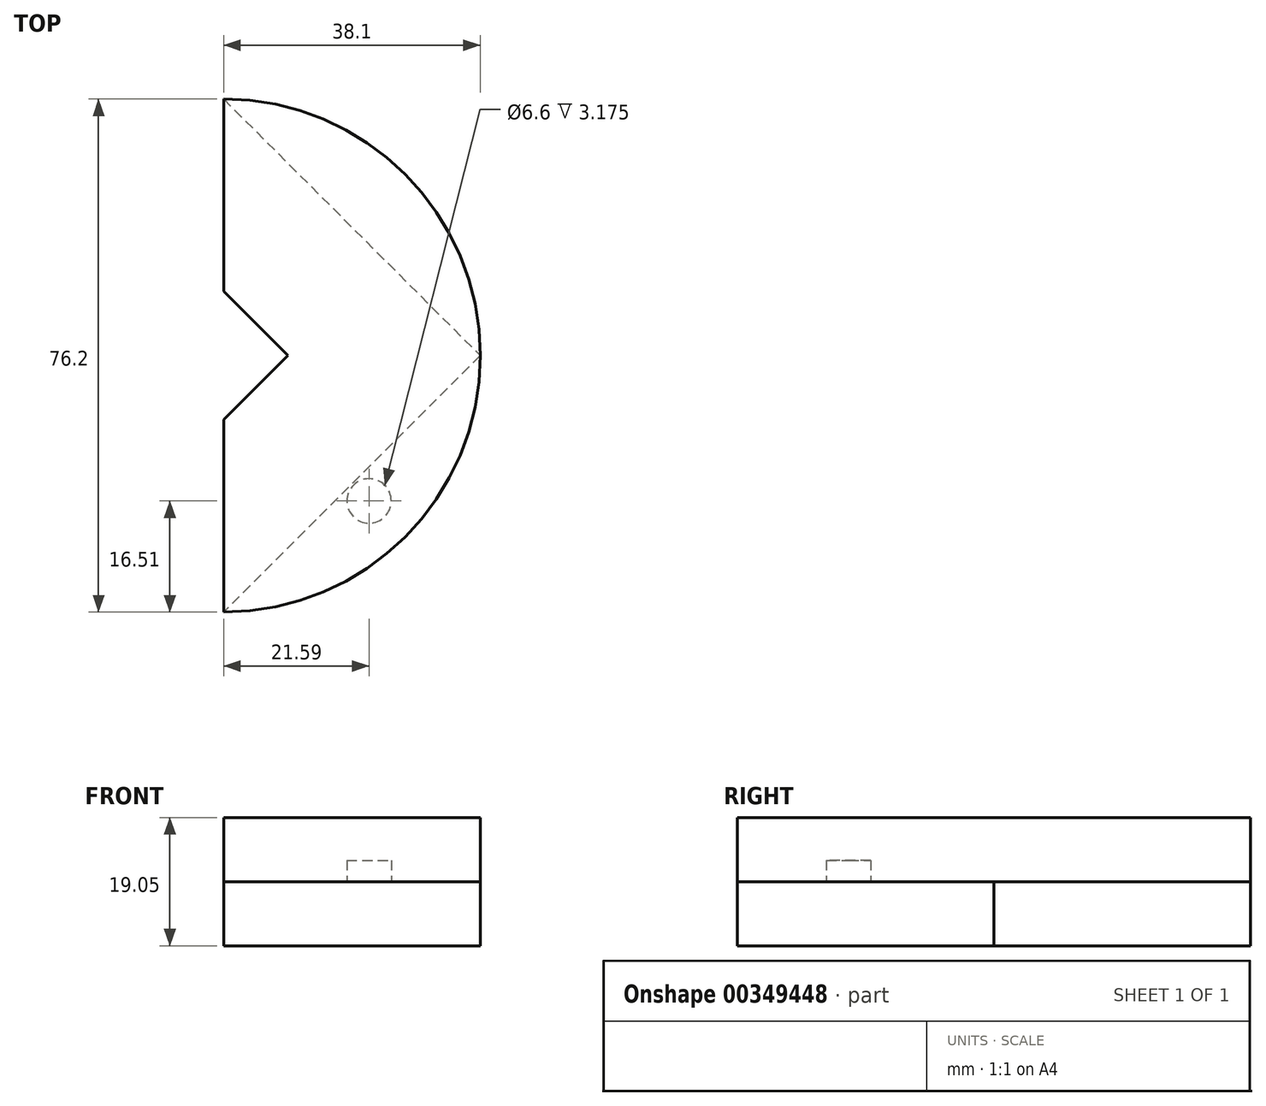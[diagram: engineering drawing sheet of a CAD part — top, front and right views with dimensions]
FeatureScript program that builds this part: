
annotation { "Feature Type Name" : "Feature", "Feature Type Description" : "" }
export const myFeature = defineFeature(function(context is Context, id is Id, definition is map)
    precondition{}
    {
        {
            var Q0;
            Q0=qCreatedBy(makeId("Top.planeOp"),FACE);
            var sketch = newSketch(context, id + "F0", { "sketchPlane" : qUnion([Q0])});
            skLineSegment(sketch, "E0", {"start": v(0, 38.1) * mm, "end": v(38.1, 0) * mm});
            skLineSegment(sketch, "E1", {"start": v(38.1, 0) * mm, "end": v(0, -38.1) * mm});
            skLineSegment(sketch, "E2", {"start": v(0, -38.1) * mm, "end": v(0, 38.1) * mm});
            skSolve(sketch);
        }
        {
            var Q0;
            Q0 = qSketchRegion(id + "F0", true);
            extrude(context, id + "F1", {"entities" : qUnion([Q0]), "depth" : 9.52 * mm});
        }
        {
            var Q0;
            Q0=makeQuery(id+"F1.opExtrude","CAP_FACE",FACE,{"disambiguationData":[OSD([sQuery(id+"F0.wireOp",EDGE,"E0"),sQuery(id+"F0.wireOp",EDGE,"E1"),sQuery(id+"F0.wireOp",EDGE,"E2")])],"isStart":false});
            var sketch = newSketch(context, id + "F2", { "sketchPlane" : qUnion([Q0])});
            skLineSegment(sketch, "E3", {"start": v(0, 38.1) * mm, "end": v(0, -38.1) * mm});
            skArc(sketch, "E4", {"start": v(0, -38.1) * mm, "mid": v(38.1, 0) * mm, "end": v(0, 38.1) * mm});
            skSolve(sketch);
        }
        {
            var Q0;
            Q0 = qSketchRegion(id + "F2", true);
            extrude(context, id + "F3", {"entities" : qUnion([Q0]), "operationType" : NewBodyOperationType.ADD, "depth" : 9.52 * mm});
        }
        {
            var Q0;
            Q0=makeQuery(id+"F1.opExtrude","CAP_FACE",FACE,{"disambiguationData":[OSD([sQuery(id+"F0.wireOp",EDGE,"E0"),sQuery(id+"F0.wireOp",EDGE,"E1"),sQuery(id+"F0.wireOp",EDGE,"E2")])],"isStart":true});
            var sketch = newSketch(context, id + "F4", { "sketchPlane" : qUnion([Q0])});
            skLineSegment(sketch, "E5", {"start": v(0, 9.52) * mm, "end": v(0, -9.53) * mm});
            skLineSegment(sketch, "E6", {"start": v(0, -9.53) * mm, "end": v(9.53, 0) * mm});
            skLineSegment(sketch, "E7", {"start": v(9.52, 0) * mm, "end": v(0, 9.53) * mm});
            skSolve(sketch);
        }
        {
            var Q0;
            Q0=makeQuery(id+"F4.imprint","IMPRINT",FACE,{"disambiguationData":[TD([[makeQuery(id+"F4.imprint","IMPRINT",EDGE,{"derivedFrom":sQuery(id+"F4.wireOp",EDGE,"E5")}),1.0]])]});
            extrude(context, id + "F5", {"entities" : qUnion([Q0]), "operationType" : NewBodyOperationType.REMOVE, "oppositeDirection" : true, "depth" : 25.4 * mm});
        }
        {
            var Q0;
            Q0=makeQuery(id+"F3.boolean.opBoolean","SPLIT",FACE,{"disambiguationData":[OD(1.0)],"derivedFrom":makeQuery(id+"F3.opExtrude","CAP_FACE",FACE,{"disambiguationData":[OSD([sQuery(id+"F2.wireOp",EDGE,"E3"),sQuery(id+"F2.wireOp",EDGE,"E4")])],"isStart":true})});
            var sketch = newSketch(context, id + "F6", { "sketchPlane" : qUnion([Q0])});
            skCircle(sketch, "E8", {"center": v(21.59, 21.59) * mm, "radius": 3.3 * mm});
            skSolve(sketch);
        }
        {
            var Q0;
            Q0=makeQuery(id+"F6.imprint","IMPRINT",FACE,{"disambiguationData":[TD([[makeQuery(id+"F6.imprint","IMPRINT",EDGE,{"derivedFrom":sQuery(id+"F6.wireOp",EDGE,"E8")}),1.0]])]});
            var Q1;
            Q1=sQuery(id+"F6.wireOp",EDGE,"E8");
            extrude(context, id + "F7", {"entities" : qUnion([Q0]), "operationType" : NewBodyOperationType.REMOVE, "surfaceEntities" : qUnion([Q1]), "oppositeDirection" : true, "depth" : 3.17 * mm});
        }
    });
